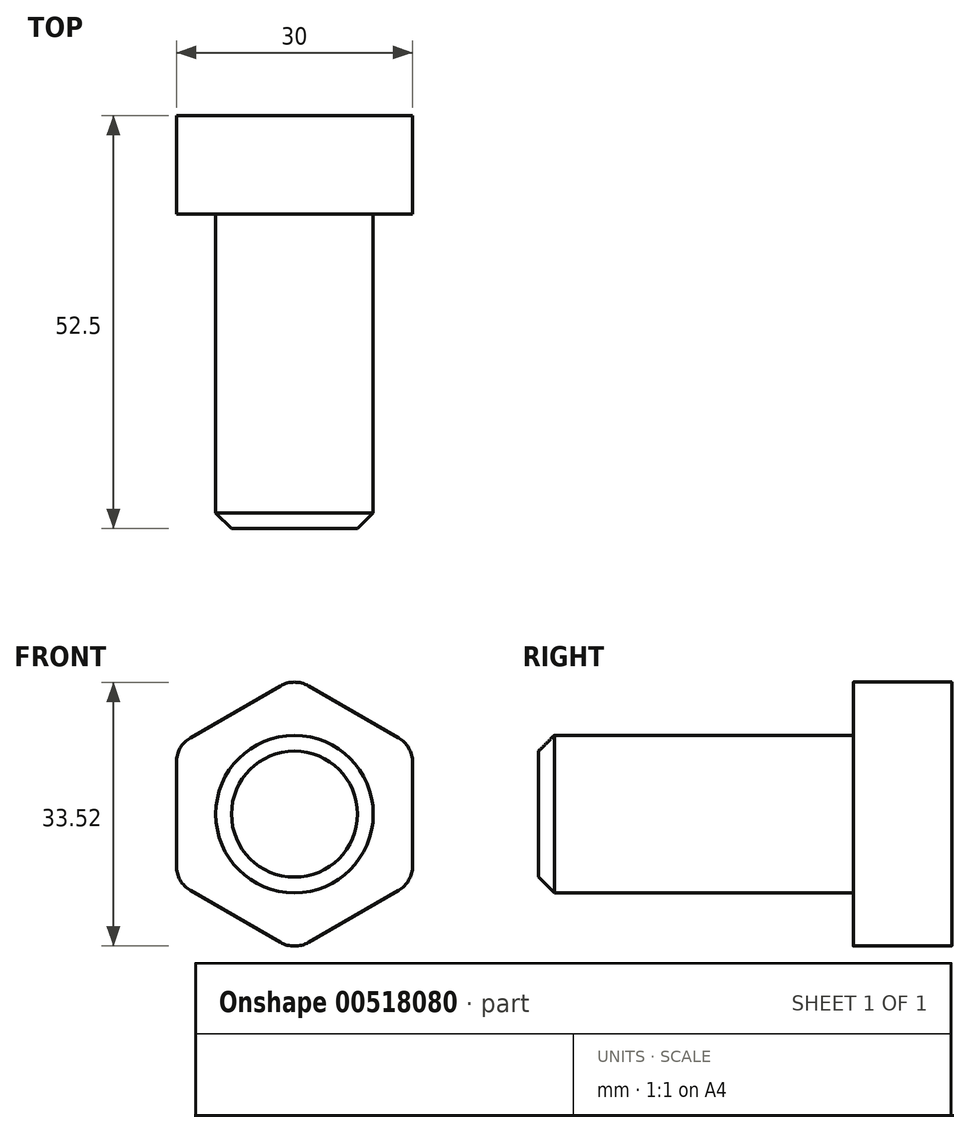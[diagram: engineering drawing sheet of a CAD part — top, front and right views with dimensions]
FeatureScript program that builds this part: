
annotation { "Feature Type Name" : "Feature", "Feature Type Description" : "" }
export const myFeature = defineFeature(function(context is Context, id is Id, definition is map)
    precondition{}
    {
        {
            var Q0;
            Q0=qCreatedBy(makeId("Right.planeOp"),FACE);
            var sketch = newSketch(context, id + "F0", { "sketchPlane" : qUnion([Q0])});
            skLineSegment(sketch, "E0", {"start": v(0, 10) * mm, "end": v(0, 25.15) * mm});
            skLineSegment(sketch, "E1", {"start": v(0, 25.15) * mm, "end": v(12.5, 25.15) * mm});
            skLineSegment(sketch, "E2", {"start": v(12.5, 25.15) * mm, "end": v(12.5, 0) * mm});
            skLineSegment(sketch, "E3", {"start": v(12.5, 0) * mm, "end": v(-40, 0) * mm});
            skLineSegment(sketch, "E4", {"start": v(-40, 0) * mm, "end": v(-40, 8) * mm});
            skLineSegment(sketch, "E5", {"start": v(-38, 10) * mm, "end": v(0, 10) * mm});
            skLineSegment(sketch, "E6", {"start": v(-40, 8) * mm, "end": v(-38, 10) * mm});
            skPoint(sketch, "E7.orphan", {"position": v(-40, 10) * mm});
            skSolve(sketch);
        }
        {
            var Q0;
            Q0=makeQuery(id+"F0.imprint","IMPRINT",FACE,{"disambiguationData":[TD([[makeQuery(id+"F0.imprint","IMPRINT",EDGE,{"derivedFrom":sQuery(id+"F0.wireOp",EDGE,"E0")}),-1.0]])]});
            var Q1;
            Q1=sQuery(id+"F0.wireOp",EDGE,"E3");
            revolve(context, id + "F1", {"entities" : qUnion([Q0]), "axis" : qUnion([Q1]), "revolveType" : RevolveType.FULL});
        }
        {
            var Q0;
            Q0=makeQuery(id+"F1.opRevolve","SWEPT_FACE",FACE,{"disambiguationData":[OSD([sQuery(id+"F0.wireOp",EDGE,"E2")])]});
            var sketch = newSketch(context, id + "F2", { "sketchPlane" : qUnion([Q0])});
            skArc(sketch, "E8", {"start": v(-1.8, -16.28) * mm, "mid": v(0, -16.77) * mm, "end": v(1.8, -16.28) * mm});
            skLineSegment(sketch, "E9", {"start": v(-1.8, -16.28) * mm, "end": v(-13.2, -9.7) * mm});
            skArc(sketch, "E10.1.0", {"start": v(13.2, -9.7) * mm, "mid": v(14.52, -8.38) * mm, "end": v(15, -6.59) * mm});
            skLineSegment(sketch, "E10.1.1", {"start": v(13.2, -9.7) * mm, "end": v(1.8, -16.28) * mm});
            skArc(sketch, "E10.2.0", {"start": v(15, 6.59) * mm, "mid": v(14.52, 8.38) * mm, "end": v(13.2, 9.7) * mm});
            skLineSegment(sketch, "E10.2.1", {"start": v(15, 6.59) * mm, "end": v(15, -6.59) * mm});
            skArc(sketch, "E10.3.0", {"start": v(1.8, 16.28) * mm, "mid": v(0, 16.77) * mm, "end": v(-1.8, 16.28) * mm});
            skLineSegment(sketch, "E10.3.1", {"start": v(1.8, 16.28) * mm, "end": v(13.2, 9.7) * mm});
            skArc(sketch, "E10.4.0", {"start": v(-13.2, 9.7) * mm, "mid": v(-14.52, 8.38) * mm, "end": v(-15, 6.59) * mm});
            skLineSegment(sketch, "E10.4.1", {"start": v(-13.2, 9.7) * mm, "end": v(-1.8, 16.28) * mm});
            skArc(sketch, "E10.5.0", {"start": v(-15, -6.59) * mm, "mid": v(-14.52, -8.38) * mm, "end": v(-13.2, -9.7) * mm});
            skLineSegment(sketch, "E10.5.1", {"start": v(-15, -6.59) * mm, "end": v(-15, 6.59) * mm});
            skPoint(sketch, "E10.center", {"position": v(0, 0) * mm});
            skSolve(sketch);
        }
        {
            var Q0;
            {var subQ0=sQuery(id+"F2.wireOp",EDGE,"ac4cea41-ed44-45b8-bd6c-50d4708beeae.4");Q0=makeQuery(id+"F2.imprint","IMPRINT",FACE,{"disambiguationData":[TD([[makeQuery(id+"F2.imprint","IMPRINT",EDGE,{"derivedFrom":subQ0}),1.0]])]});}
            var Q1;
            {var subQ0=sQuery(id+"F2.wireOp",EDGE,"ac4cea41-ed44-45b8-bd6c-50d4708beeae.5");Q1=makeQuery(id+"F2.imprint","IMPRINT",FACE,{"disambiguationData":[TD([[makeQuery(id+"F2.imprint","IMPRINT",EDGE,{"derivedFrom":subQ0}),1.0]])]});}
            var Q2;
            {var subQ0=sQuery(id+"F2.wireOp",EDGE,"ac4cea41-ed44-45b8-bd6c-50d4708beeae.0");Q2=makeQuery(id+"F2.imprint","IMPRINT",FACE,{"disambiguationData":[TD([[makeQuery(id+"F2.imprint","IMPRINT",EDGE,{"derivedFrom":subQ0}),1.0]])]});}
            var Q3;
            {var subQ0=sQuery(id+"F2.wireOp",EDGE,"ac4cea41-ed44-45b8-bd6c-50d4708beeae.1");Q3=makeQuery(id+"F2.imprint","IMPRINT",FACE,{"disambiguationData":[TD([[makeQuery(id+"F2.imprint","IMPRINT",EDGE,{"derivedFrom":subQ0}),1.0]])]});}
            var Q4;
            {var subQ0=sQuery(id+"F2.wireOp",EDGE,"ac4cea41-ed44-45b8-bd6c-50d4708beeae.2");Q4=makeQuery(id+"F2.imprint","IMPRINT",FACE,{"disambiguationData":[TD([[makeQuery(id+"F2.imprint","IMPRINT",EDGE,{"derivedFrom":subQ0}),1.0]])]});}
            var Q5;
            {var subQ0=sQuery(id+"F2.wireOp",EDGE,"ac4cea41-ed44-45b8-bd6c-50d4708beeae.3");Q5=makeQuery(id+"F2.imprint","IMPRINT",FACE,{"disambiguationData":[TD([[makeQuery(id+"F2.imprint","IMPRINT",EDGE,{"derivedFrom":subQ0}),1.0]])]});}
            var Q6;
            Q6=makeQuery(id+"F2.imprint","IMPRINT",FACE,{"disambiguationData":[TD([[makeQuery(id+"F2.imprint","IMPRINT",EDGE,{"derivedFrom":sQuery(id+"F2.wireOp",EDGE,"E8")}),-1.0]])]});
            extrude(context, id + "F3", {"entities" : qUnion([Q0, Q1, Q2, Q3, Q4, Q5, Q6]), "operationType" : NewBodyOperationType.REMOVE, "oppositeDirection" : true, "depth" : 25 * mm, "offsetDistance" : 25 * mm});
        }
    });
